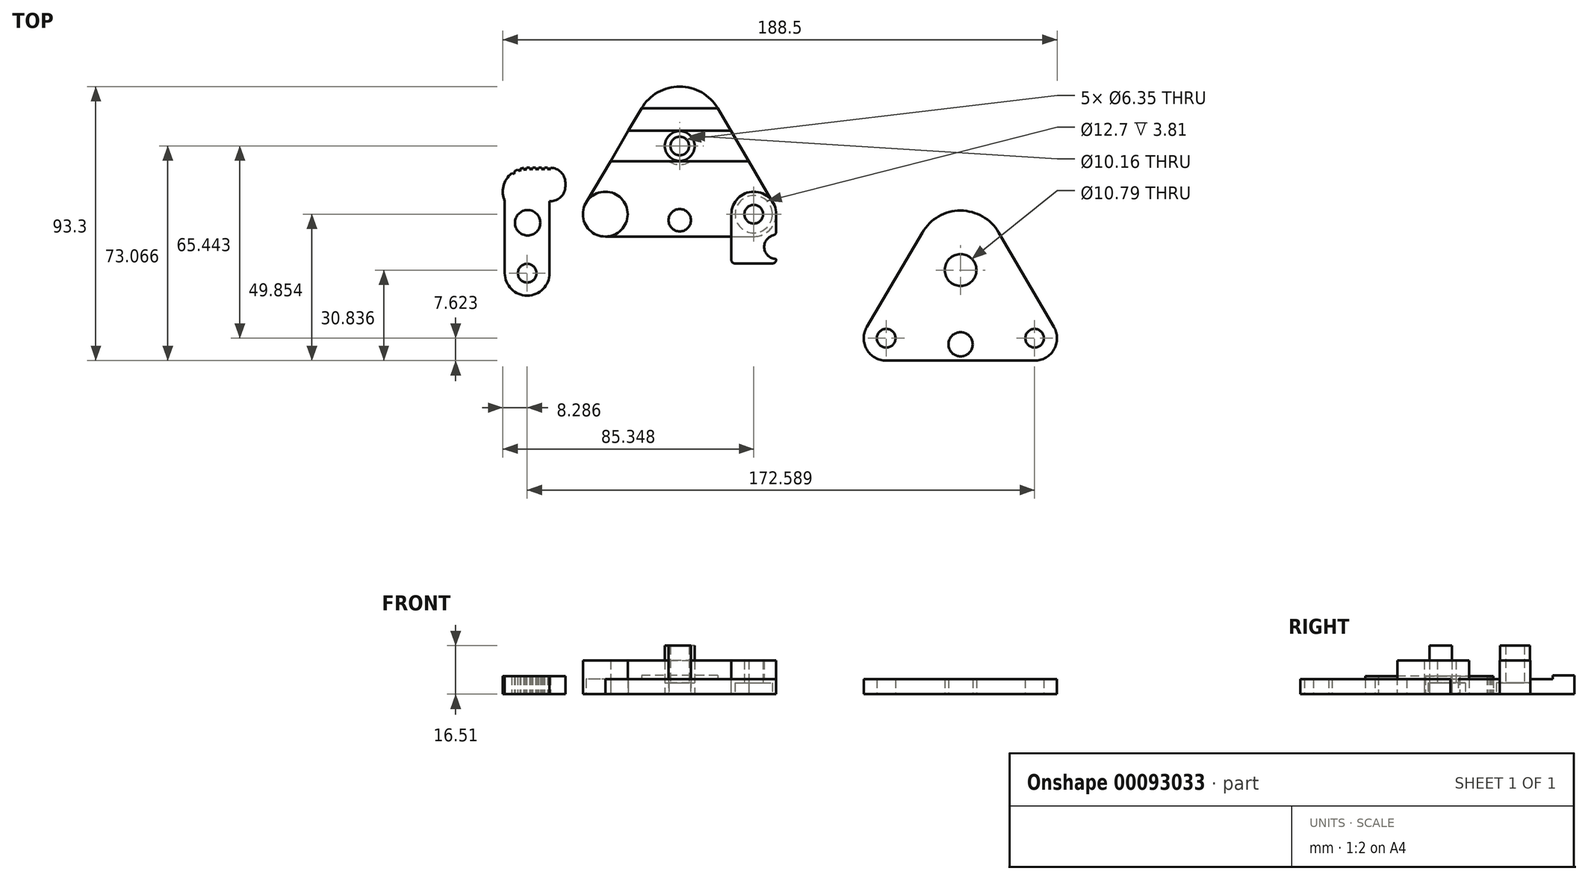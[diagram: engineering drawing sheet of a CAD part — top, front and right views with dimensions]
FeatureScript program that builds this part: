
annotation { "Feature Type Name" : "Feature", "Feature Type Description" : "" }
export const myFeature = defineFeature(function(context is Context, id is Id, definition is map)
    precondition{}
    {
        {
            var Q0;
            Q0=qCreatedBy(makeId("Top.planeOp"),FACE);
            var sketch = newSketch(context, id + "F0", { "sketchPlane" : qUnion([Q0])});
            skPoint(sketch, "E0.middle", {"position": v(0, 0) * mm});
            skLineSegment(sketch, "E1", {"start": v(-25.32, -38.25) * mm, "end": v(25.18, -38.25) * mm});
            skLineSegment(sketch, "E2", {"start": v(31.76, -26.78) * mm, "end": v(12.96, 5.36) * mm});
            skLineSegment(sketch, "E3", {"start": v(-13, 5.39) * mm, "end": v(-31.89, -26.77) * mm});
            skPoint(sketch, "E4.visualSharp", {"position": v(-38.63, -38.25) * mm});
            skArc(sketch, "E4.filletArc", {"start": v(-31.89, -26.77) * mm, "mid": v(-31.93, -34.41) * mm, "end": v(-25.32, -38.25) * mm});
            skPoint(sketch, "E5.visualSharp", {"position": v(38.46, -38.25) * mm});
            skArc(sketch, "E5.filletArc", {"start": v(25.18, -38.25) * mm, "mid": v(31.79, -34.42) * mm, "end": v(31.76, -26.78) * mm});
            skPoint(sketch, "E6.visualSharp", {"position": v(0, 27.54) * mm});
            skArc(sketch, "E6.filletArc", {"start": v(12.96, 5.36) * mm, "mid": v(-0.01, 12.82) * mm, "end": v(-13, 5.39) * mm});
            skLineSegment(sketch, "E7", {"start": v(12.96, 5.36) * mm, "end": v(-13, 5.39) * mm});
            skPoint(sketch, "E8", {"position": v(0, -2.24) * mm});
            skLineSegment(sketch, "E9", {"start": v(-17.48, -2.23) * mm, "end": v(17.41, -2.24) * mm});
            skPoint(sketch, "E10", {"position": v(0, -12.58) * mm});
            skCircle(sketch, "E11", {"center": v(0, -32.68) * mm, "radius": 3.81 * mm});
            skCircle(sketch, "E12", {"center": v(25.18, -30.63) * mm, "radius": 3.18 * mm});
            skCircle(sketch, "E13", {"center": v(-25.32, -30.63) * mm, "radius": 3.18 * mm});
            skLineSegment(sketch, "E14", {"start": v(-7.77, -25.38) * mm, "end": v(7.27, -25.38) * mm, "construction": true});
            skLineSegment(sketch, "E15", {"start": v(-0.37, -13.98) * mm, "end": v(-0.82, -14.9) * mm, "construction": true});
            skLineSegment(sketch, "E16", {"start": v(-0.82, -14.9) * mm, "end": v(-1.4, -14.06) * mm, "construction": true});
            skLineSegment(sketch, "E17", {"start": v(-2.4, -14.27) * mm, "end": v(-2.63, -15.26) * mm, "construction": true});
            skLineSegment(sketch, "E18", {"start": v(-2.63, -15.26) * mm, "end": v(-3.42, -14.62) * mm, "construction": true});
            skLineSegment(sketch, "E19", {"start": v(-4.44, -15.13) * mm, "end": v(-4.48, -16.14) * mm, "construction": true});
            skLineSegment(sketch, "E20", {"start": v(-4.48, -16.14) * mm, "end": v(-5.45, -15.84) * mm, "construction": true});
            skArc(sketch, "E21.trimOffspring", {"start": v(-1.4, -14.06) * mm, "mid": v(-1.9, -14.15) * mm, "end": v(-2.4, -14.27) * mm, "construction": true});
            skArc(sketch, "E22.trimOffspring", {"start": v(-3.42, -14.62) * mm, "mid": v(-3.94, -14.85) * mm, "end": v(-4.44, -15.13) * mm, "construction": true});
            skArc(sketch, "E23.trimOffspring", {"start": v(-5.45, -15.84) * mm, "mid": v(-8.2, -20.23) * mm, "end": v(-7.77, -25.38) * mm, "construction": true});
            skLineSegment(sketch, "E24", {"start": v(7.27, -25.38) * mm, "end": v(7.73, -25.38) * mm, "construction": true});
            skLineSegment(sketch, "E25", {"start": v(12.81, -20.3) * mm, "end": v(12.81, -19.06) * mm, "construction": true});
            skLineSegment(sketch, "E26", {"start": v(0, -13.98) * mm, "end": v(0.64, -13.98) * mm, "construction": true});
            skArc(sketch, "E27.filletArc", {"start": v(12.81, -19.06) * mm, "mid": v(11.32, -15.47) * mm, "end": v(7.73, -13.98) * mm, "construction": true});
            skLineSegment(sketch, "E28", {"start": v(-0.37, -13.98) * mm, "end": v(0, -13.98) * mm, "construction": true});
            skLineSegment(sketch, "E29", {"start": v(0.64, -13.98) * mm, "end": v(1.15, -14.86) * mm, "construction": true});
            skLineSegment(sketch, "E30", {"start": v(1.15, -14.86) * mm, "end": v(1.66, -13.98) * mm, "construction": true});
            skLineSegment(sketch, "E31", {"start": v(2.67, -13.98) * mm, "end": v(3.18, -14.86) * mm, "construction": true});
            skLineSegment(sketch, "E32", {"start": v(3.18, -14.86) * mm, "end": v(3.69, -13.98) * mm, "construction": true});
            skLineSegment(sketch, "E33", {"start": v(4.7, -13.98) * mm, "end": v(5.21, -14.86) * mm, "construction": true});
            skLineSegment(sketch, "E34", {"start": v(5.21, -14.86) * mm, "end": v(5.72, -13.98) * mm, "construction": true});
            skLineSegment(sketch, "E35", {"start": v(6.74, -13.98) * mm, "end": v(7.25, -14.86) * mm, "construction": true});
            skLineSegment(sketch, "E36", {"start": v(7.25, -14.86) * mm, "end": v(7.75, -13.98) * mm, "construction": true});
            skLineSegment(sketch, "E37.trimOffspring", {"start": v(5.72, -13.98) * mm, "end": v(6.74, -13.98) * mm, "construction": true});
            skLineSegment(sketch, "E38.trimOffspring", {"start": v(3.69, -13.98) * mm, "end": v(4.7, -13.98) * mm, "construction": true});
            skLineSegment(sketch, "E39.trimOffspring", {"start": v(1.66, -13.98) * mm, "end": v(2.67, -13.98) * mm, "construction": true});
            skLineSegment(sketch, "E40.bottom", {"start": v(-7.77, -25.38) * mm, "end": v(7.47, -25.38) * mm, "construction": true});
            skLineSegment(sketch, "E40.top", {"start": v(-0.15, -57.3) * mm, "end": v(-0.15, -57.3) * mm});
            skLineSegment(sketch, "E40.left", {"start": v(-7.77, -25.38) * mm, "end": v(-7.77, -49.68) * mm, "construction": true});
            skLineSegment(sketch, "E40.right", {"start": v(7.47, -25.38) * mm, "end": v(7.47, -49.68) * mm, "construction": true});
            skLineSegment(sketch, "E41", {"start": v(-23.56, -12.58) * mm, "end": v(23.46, -12.58) * mm});
            skPoint(sketch, "E42.visualSharp", {"position": v(12.81, -25.38) * mm});
            skArc(sketch, "E42.filletArc", {"start": v(7.73, -25.38) * mm, "mid": v(11.32, -23.9) * mm, "end": v(12.81, -20.3) * mm, "construction": true});
            skCircle(sketch, "E43", {"center": v(0, -32.68) * mm, "radius": 4.32 * mm, "construction": true});
            skPoint(sketch, "E44.visualSharp", {"position": v(-7.77, -57.3) * mm});
            skArc(sketch, "E44.filletArc", {"start": v(-7.77, -49.68) * mm, "mid": v(-5.53, -55.06) * mm, "end": v(-0.15, -57.3) * mm, "construction": true});
            skPoint(sketch, "E45.visualSharp", {"position": v(7.47, -57.3) * mm});
            skArc(sketch, "E45.filletArc", {"start": v(-0.15, -57.3) * mm, "mid": v(5.24, -55.06) * mm, "end": v(7.47, -49.68) * mm, "construction": true});
            skCircle(sketch, "E46", {"center": v(-0.15, -49.68) * mm, "radius": 3.18 * mm, "construction": true});
            skCircle(sketch, "E47", {"center": v(25.18, -30.63) * mm, "radius": 7.62 * mm});
            skCircle(sketch, "E48", {"center": v(-25.32, -30.63) * mm, "radius": 7.62 * mm});
            skPoint(sketch, "E49", {"position": v(0, -7.41) * mm});
            skCircle(sketch, "E50", {"center": v(0, -7.41) * mm, "radius": 3.18 * mm});
            skLineSegment(sketch, "E51", {"start": v(32.8, -30.63) * mm, "end": v(32.8, -36.58) * mm});
            skLineSegment(sketch, "E52", {"start": v(31.53, -47.41) * mm, "end": v(18.83, -47.41) * mm});
            skLineSegment(sketch, "E53", {"start": v(17.56, -30.63) * mm, "end": v(17.56, -46.14) * mm});
            skArc(sketch, "E54", {"start": v(31.83, -37.81) * mm, "mid": v(28.74, -42.14) * mm, "end": v(32.56, -45.83) * mm});
            skLineSegment(sketch, "E55.trimOffspring", {"start": v(32.8, -46.09) * mm, "end": v(32.8, -46.14) * mm});
            skPoint(sketch, "E56.visualSharp", {"position": v(17.56, -47.41) * mm});
            skArc(sketch, "E56.filletArc", {"start": v(17.56, -46.14) * mm, "mid": v(17.93, -47.04) * mm, "end": v(18.83, -47.41) * mm});
            skPoint(sketch, "E57.visualSharp", {"position": v(32.8, -47.41) * mm});
            skArc(sketch, "E57.filletArc", {"start": v(31.53, -47.41) * mm, "mid": v(32.43, -47.04) * mm, "end": v(32.8, -46.14) * mm});
            skPoint(sketch, "E58.visualSharp", {"position": v(32.8, -37.7) * mm});
            skArc(sketch, "E58.filletArc", {"start": v(31.83, -37.81) * mm, "mid": v(32.53, -37.36) * mm, "end": v(32.8, -36.58) * mm});
            skPoint(sketch, "E59.visualSharp", {"position": v(32.8, -45.84) * mm});
            skArc(sketch, "E59.filletArc", {"start": v(32.8, -46.09) * mm, "mid": v(32.73, -45.91) * mm, "end": v(32.56, -45.83) * mm});
            skCircle(sketch, "E60", {"center": v(0, -7.41) * mm, "radius": 5.08 * mm});
            skSolve(sketch);
        }
        {
            var Q0;
            Q0=makeQuery(id+"F0.imprint","IMPRINT",FACE,{"disambiguationData":[TD([[makeQuery(id+"F0.imprint","IMPRINT",EDGE,{"derivedFrom":sQuery(id+"F0.wireOp",EDGE,"E11")}),-1.0]])]});
            var sketch = newSketch(context, id + "F1", { "sketchPlane" : qUnion([Q0])});
            skLineSegment(sketch, "E61", {"start": v(-59.5, -26.24) * mm, "end": v(-44.47, -26.24) * mm});
            skLineSegment(sketch, "E62", {"start": v(-52.11, -14.83) * mm, "end": v(-52.55, -15.75) * mm});
            skLineSegment(sketch, "E63", {"start": v(-52.55, -15.75) * mm, "end": v(-53.13, -14.91) * mm});
            skLineSegment(sketch, "E64", {"start": v(-54.15, -15.12) * mm, "end": v(-54.37, -16.11) * mm});
            skLineSegment(sketch, "E65", {"start": v(-54.37, -16.11) * mm, "end": v(-55.16, -15.47) * mm});
            skLineSegment(sketch, "E66", {"start": v(-56.18, -15.98) * mm, "end": v(-56.22, -17) * mm});
            skLineSegment(sketch, "E67", {"start": v(-56.22, -17) * mm, "end": v(-57.2, -16.7) * mm});
            skArc(sketch, "E68.trimOffspring", {"start": v(-53.13, -14.91) * mm, "mid": v(-53.64, -15) * mm, "end": v(-54.15, -15.12) * mm});
            skArc(sketch, "E69.trimOffspring", {"start": v(-55.16, -15.47) * mm, "mid": v(-55.68, -15.7) * mm, "end": v(-56.18, -15.98) * mm});
            skArc(sketch, "E70.trimOffspring", {"start": v(-57.2, -16.7) * mm, "mid": v(-59.94, -21.08) * mm, "end": v(-59.5, -26.24) * mm});
            skLineSegment(sketch, "E71", {"start": v(-44.47, -26.24) * mm, "end": v(-44, -26.24) * mm});
            skLineSegment(sketch, "E72", {"start": v(-38.93, -21.16) * mm, "end": v(-38.93, -19.91) * mm});
            skLineSegment(sketch, "E73", {"start": v(-51.74, -14.83) * mm, "end": v(-51.1, -14.83) * mm});
            skArc(sketch, "E74.filletArc", {"start": v(-38.93, -19.91) * mm, "mid": v(-40.42, -16.32) * mm, "end": v(-44, -14.83) * mm});
            skLineSegment(sketch, "E75", {"start": v(-52.11, -14.83) * mm, "end": v(-51.74, -14.83) * mm});
            skLineSegment(sketch, "E76", {"start": v(-51.1, -14.83) * mm, "end": v(-50.59, -15.71) * mm});
            skLineSegment(sketch, "E77", {"start": v(-50.59, -15.71) * mm, "end": v(-50.08, -14.83) * mm});
            skLineSegment(sketch, "E78", {"start": v(-49.07, -14.83) * mm, "end": v(-48.56, -15.71) * mm});
            skLineSegment(sketch, "E79", {"start": v(-48.56, -15.71) * mm, "end": v(-48.05, -14.83) * mm});
            skLineSegment(sketch, "E80", {"start": v(-47.03, -14.83) * mm, "end": v(-46.53, -15.71) * mm});
            skLineSegment(sketch, "E81", {"start": v(-46.53, -15.71) * mm, "end": v(-46.02, -14.83) * mm});
            skLineSegment(sketch, "E82", {"start": v(-45, -14.83) * mm, "end": v(-44.5, -15.71) * mm});
            skLineSegment(sketch, "E83", {"start": v(-44.5, -15.71) * mm, "end": v(-43.99, -14.83) * mm});
            skLineSegment(sketch, "E84.trimOffspring", {"start": v(-46.02, -14.83) * mm, "end": v(-45, -14.83) * mm});
            skLineSegment(sketch, "E85.trimOffspring", {"start": v(-48.05, -14.83) * mm, "end": v(-47.03, -14.83) * mm});
            skLineSegment(sketch, "E86.trimOffspring", {"start": v(-50.08, -14.83) * mm, "end": v(-49.07, -14.83) * mm});
            skLineSegment(sketch, "E87.bottom", {"start": v(-59.5, -26.24) * mm, "end": v(-44.26, -26.24) * mm});
            skLineSegment(sketch, "E87.left", {"start": v(-59.5, -26.24) * mm, "end": v(-59.5, -50.71) * mm});
            skLineSegment(sketch, "E87.right", {"start": v(-44.26, -26.24) * mm, "end": v(-44.26, -50.71) * mm});
            skPoint(sketch, "E88.visualSharp", {"position": v(-38.93, -26.24) * mm});
            skArc(sketch, "E88.filletArc", {"start": v(-44, -26.24) * mm, "mid": v(-40.42, -24.75) * mm, "end": v(-38.93, -21.16) * mm});
            skCircle(sketch, "E89", {"center": v(-51.74, -33.55) * mm, "radius": 4.32 * mm});
            skPoint(sketch, "E90.visualSharp", {"position": v(-59.5, -58.33) * mm});
            skArc(sketch, "E90.filletArc", {"start": v(-59.5, -50.71) * mm, "mid": v(-57.27, -56.1) * mm, "end": v(-51.88, -58.33) * mm});
            skPoint(sketch, "E91.visualSharp", {"position": v(-44.26, -58.33) * mm});
            skArc(sketch, "E91.filletArc", {"start": v(-51.88, -58.33) * mm, "mid": v(-46.5, -56.1) * mm, "end": v(-44.26, -50.71) * mm});
            skCircle(sketch, "E92", {"center": v(-51.88, -50.71) * mm, "radius": 3.18 * mm});
            skSolve(sketch);
        }
        {
            var Q0;
            Q0=makeQuery(id+"F0.imprint","IMPRINT",FACE,{"disambiguationData":[TD([[makeQuery(id+"F0.imprint","IMPRINT",EDGE,{"derivedFrom":sQuery(id+"F0.wireOp",EDGE,"E11")}),-1.0]])]});
            var Q1;
            {var subQ0=sQuery(id+"F0.wireOp",EDGE,"E7");Q1=makeQuery(id+"F0.imprint","IMPRINT",FACE,{"disambiguationData":[TD([[makeQuery(id+"F0.imprint","IMPRINT",EDGE,{"derivedFrom":subQ0}),1.0]])]});}
            var Q2;
            {var subQ0=sQuery(id+"F0.wireOp",EDGE,"E47");var subQ1=sQuery(id+"F0.wireOp",EDGE,"E1");var subQ2=makeQuery(id+"F0.imprint","INTERSECT",VERTEX,{"derivedFrom":[subQ1,subQ0]});Q2=makeQuery(id+"F0.imprint","IMPRINT",FACE,{"disambiguationData":[TD([[makeQuery(id+"F0.imprint","IMPRINT",EDGE,{"disambiguationData":[TD([[subQ2,1.0]])],"derivedFrom":subQ1}),1.0]])]});}
            extrude(context, id + "F2", {"entities" : qUnion([Q0, Q1, Q2]), "depth" : 5.08 * mm});
        }
        {
            var Q0;
            {var subQ1=sQuery(id+"F0.wireOp",EDGE,"E9");Q0=makeQuery(id+"F0.imprint","IMPRINT",FACE,{"disambiguationData":[TD([[makeQuery(id+"F0.imprint","IMPRINT",EDGE,{"derivedFrom":subQ1}),-1.0]])]});}
            var Q1;
            Q1=makeQuery(id+"F0.imprint","IMPRINT",FACE,{"disambiguationData":[TD([[makeQuery(id+"F0.imprint","IMPRINT",EDGE,{"derivedFrom":sQuery(id+"F0.wireOp",EDGE,"E13")}),-1.0]])]});
            var Q2;
            Q2=makeQuery(id+"F0.imprint","IMPRINT",FACE,{"disambiguationData":[TD([[makeQuery(id+"F0.imprint","IMPRINT",EDGE,{"derivedFrom":sQuery(id+"F0.wireOp",EDGE,"E12")}),-1.0]])]});
            var Q3;
            {var subQ0=sQuery(id+"F0.wireOp",EDGE,"E47");var subQ1=sQuery(id+"F0.wireOp",EDGE,"E1");var subQ2=makeQuery(id+"F0.imprint","INTERSECT",VERTEX,{"derivedFrom":[subQ1,subQ0]});Q3=makeQuery(id+"F0.imprint","IMPRINT",FACE,{"disambiguationData":[TD([[makeQuery(id+"F0.imprint","IMPRINT",EDGE,{"disambiguationData":[TD([[subQ2,1.0]])],"derivedFrom":subQ1}),1.0]])]});}
            var Q4;
            Q4=makeQuery(id+"F0.imprint","IMPRINT",FACE,{"disambiguationData":[TD([[makeQuery(id+"F0.imprint","IMPRINT",EDGE,{"derivedFrom":sQuery(id+"F0.wireOp",EDGE,"E12")}),1.0]])]});
            var Q5;
            Q5=makeQuery(id+"F0.imprint","IMPRINT",FACE,{"disambiguationData":[TD([[makeQuery(id+"F0.imprint","IMPRINT",EDGE,{"derivedFrom":sQuery(id+"F0.wireOp",EDGE,"E13")}),1.0]])]});
            extrude(context, id + "F3", {"entities" : qUnion([Q0, Q1, Q2, Q3, Q4, Q5]), "depth" : 11.43 * mm});
        }
        {
            var Q0;
            Q0=makeQuery(id+"F0.imprint","IMPRINT",FACE,{"disambiguationData":[TD([[makeQuery(id+"F0.imprint","IMPRINT",EDGE,{"derivedFrom":sQuery(id+"F0.wireOp",EDGE,"E11")}),1.0]])]});
            var Q1;
            Q1=makeQuery(id+"F0.imprint","IMPRINT",FACE,{"disambiguationData":[TD([[makeQuery(id+"F0.imprint","IMPRINT",EDGE,{"derivedFrom":sQuery(id+"F0.wireOp",EDGE,"E50")}),-1.0]])]});
            var Q2;
            Q2=makeQuery(id+"F0.imprint","IMPRINT",FACE,{"disambiguationData":[TD([[makeQuery(id+"F0.imprint","IMPRINT",EDGE,{"derivedFrom":sQuery(id+"F0.wireOp",EDGE,"E50")}),1.0]])]});
            extrude(context, id + "F4", {"entities" : qUnion([Q0, Q1, Q2]), "depth" : 16.5 * mm});
        }
        {
            var Q0;
            Q0=makeQuery(id+"F0.imprint","IMPRINT",FACE,{"disambiguationData":[TD([[makeQuery(id+"F0.imprint","IMPRINT",EDGE,{"derivedFrom":sQuery(id+"F0.wireOp",EDGE,"E6.filletArc")}),1.0]])]});
            extrude(context, id + "F5", {"entities" : qUnion([Q0]), "operationType" : NewBodyOperationType.ADD, "depth" : 6.35 * mm});
        }
        {
            var Q0;
            {var subQ3=sQuery(id+"F0.wireOp",EDGE,"E51");Q0=makeQuery(id+"F0.imprint","IMPRINT",FACE,{"disambiguationData":[TD([[makeQuery(id+"F0.imprint","IMPRINT",EDGE,{"derivedFrom":subQ3}),-1.0]])]});}
            extrude(context, id + "F6", {"entities" : qUnion([Q0]), "operationType" : NewBodyOperationType.ADD, "depth" : 11.43 * mm, "hasSecondDirection" : true, "secondDirectionOppositeDirection" : false, "secondDirectionDepth" : 5.08 * mm});
        }
        {
            var Q0;
            Q0=makeQuery(id+"F1.imprint","IMPRINT",FACE,{"disambiguationData":[TD([[makeQuery(id+"F1.imprint","IMPRINT",EDGE,{"derivedFrom":sQuery(id+"F1.wireOp",EDGE,"E62")}),1.0]])]});
            var Q1;
            {var subQ3=sQuery(id+"F1.wireOp",EDGE,"E87.left");Q1=makeQuery(id+"F1.imprint","IMPRINT",FACE,{"disambiguationData":[TD([[makeQuery(id+"F1.imprint","IMPRINT",EDGE,{"derivedFrom":subQ3}),1.0]])]});}
            extrude(context, id + "F7", {"entities" : qUnion([Q0, Q1]), "depth" : 6.1 * mm});
        }
        {
            var Q0;
            Q0=qCreatedBy(makeId("Top.planeOp"),FACE);
            var sketch = newSketch(context, id + "F8", { "sketchPlane" : qUnion([Q0])});
            skLineSegment(sketch, "E93", {"start": v(70.21, -80.48) * mm, "end": v(120.7, -80.48) * mm});
            skLineSegment(sketch, "E94", {"start": v(127.28, -69.01) * mm, "end": v(108.5, -36.87) * mm});
            skLineSegment(sketch, "E95", {"start": v(82.52, -36.84) * mm, "end": v(63.64, -69) * mm});
            skPoint(sketch, "E96.visualSharp", {"position": v(56.9, -80.48) * mm});
            skArc(sketch, "E96.filletArc", {"start": v(63.64, -69) * mm, "mid": v(63.6, -76.64) * mm, "end": v(70.21, -80.48) * mm});
            skPoint(sketch, "E97.visualSharp", {"position": v(133.99, -80.48) * mm});
            skArc(sketch, "E97.filletArc", {"start": v(120.7, -80.48) * mm, "mid": v(127.32, -76.65) * mm, "end": v(127.28, -69.01) * mm});
            skPoint(sketch, "E98.visualSharp", {"position": v(95.53, -14.7) * mm});
            skArc(sketch, "E98.filletArc", {"start": v(108.5, -36.87) * mm, "mid": v(95.51, -29.41) * mm, "end": v(82.52, -36.84) * mm});
            skCircle(sketch, "E99", {"center": v(95.53, -74.91) * mm, "radius": 4.13 * mm});
            skCircle(sketch, "E100", {"center": v(120.7, -72.86) * mm, "radius": 3.18 * mm});
            skCircle(sketch, "E101", {"center": v(70.21, -72.86) * mm, "radius": 3.18 * mm});
            skPoint(sketch, "E102", {"position": v(95.53, -49.64) * mm});
            skPoint(sketch, "E103.visualSharp", {"position": v(128.33, -79.93) * mm});
            skCircle(sketch, "E104", {"center": v(95.53, -49.64) * mm, "radius": 5.4 * mm});
            skPoint(sketch, "E105.end.orphan", {"position": v(112.94, -44.48) * mm});
            skPoint(sketch, "E105.start.orphan", {"position": v(78.05, -44.46) * mm});
            skPoint(sketch, "E106.orphan", {"position": v(71.97, -54.81) * mm});
            skPoint(sketch, "E107.end.orphan", {"position": v(118.98, -54.81) * mm});
            skSolve(sketch);
        }
        {
            var Q0;
            {var subQ1=sQuery(id+"F8.wireOp",EDGE,"216794e6-27fa-4e69-877c-28185c22a6c9");Q0=makeQuery(id+"F8.imprint","IMPRINT",FACE,{"disambiguationData":[TD([[makeQuery(id+"F8.imprint","IMPRINT",EDGE,{"derivedFrom":subQ1}),1.0]])]});}
            var Q1;
            {var subQ1=sQuery(id+"F8.wireOp",EDGE,"bfd4ebca-ad6c-44b5-a8af-35f49ae3cf0c");Q1=makeQuery(id+"F8.imprint","IMPRINT",FACE,{"disambiguationData":[TD([[makeQuery(id+"F8.imprint","IMPRINT",EDGE,{"derivedFrom":subQ1}),1.0]])]});}
            var Q2;
            Q2=makeQuery(id+"F8.imprint","IMPRINT",FACE,{"disambiguationData":[TD([[makeQuery(id+"F8.imprint","IMPRINT",EDGE,{"derivedFrom":makeQuery(id+"F3.opExtrude","CAP_EDGE",EDGE,{"disambiguationData":[OSD([sQuery(id+"F0.wireOp",EDGE,"E50")])],"isStart":false})}),1.0]])]});
            var Q3;
            Q3=makeQuery(id+"F8.imprint","IMPRINT",FACE,{"disambiguationData":[TD([[makeQuery(id+"F8.imprint","IMPRINT",EDGE,{"derivedFrom":sQuery(id+"F8.wireOp",EDGE,"b530ac93-75ae-482a-9c66-041d02c707ac")}),-1.0]])]});
            var Q4;
            {var subQ0=sQuery(id+"F8.wireOp",EDGE,"d28c21e8-73c2-4f8c-b565-6b58b0dd52e0");var subQ1=makeQuery(id+"F3.opExtrude","CAP_EDGE",EDGE,{"disambiguationData":[OSD([sQuery(id+"F0.wireOp",EDGE,"E2")])],"isStart":false});var subQ2=makeQuery(id+"F8.imprint","INTERSECT",VERTEX,{"derivedFrom":[subQ1,subQ0]});Q4=makeQuery(id+"F8.imprint","IMPRINT",FACE,{"disambiguationData":[TD([[makeQuery(id+"F8.imprint","IMPRINT",EDGE,{"disambiguationData":[TD([[subQ2,-1.0]])],"derivedFrom":subQ0}),1.0]])]});}
            var Q5;
            Q5=makeQuery(id+"F8.imprint","IMPRINT",FACE,{"disambiguationData":[TD([[makeQuery(id+"F8.imprint","IMPRINT",EDGE,{"derivedFrom":sQuery(id+"F8.wireOp",EDGE,"48c16e6e-6f29-480b-870d-e4ed0377c5a1")}),-1.0]])]});
            var Q6;
            {var subQ0=sQuery(id+"F8.wireOp",EDGE,"bfb3cdb1-9707-4c23-9635-bff32e19fff3");var subQ1=makeQuery(id+"F3.opExtrude","CAP_EDGE",EDGE,{"disambiguationData":[OSD([sQuery(id+"F0.wireOp",EDGE,"E3")])],"isStart":false});var subQ2=makeQuery(id+"F8.imprint","INTERSECT",VERTEX,{"derivedFrom":[subQ1,subQ0]});Q6=makeQuery(id+"F8.imprint","IMPRINT",FACE,{"disambiguationData":[TD([[makeQuery(id+"F8.imprint","IMPRINT",EDGE,{"disambiguationData":[TD([[subQ2,1.0]])],"derivedFrom":subQ0}),1.0]])]});}
            var Q7;
            Q7=makeQuery(id+"F8.imprint","IMPRINT",FACE,{"disambiguationData":[TD([[makeQuery(id+"F8.imprint","IMPRINT",EDGE,{"derivedFrom":sQuery(id+"F8.wireOp",EDGE,"E93")}),1.0]])]});
            extrude(context, id + "F9", {"entities" : qUnion([Q0, Q1, Q2, Q3, Q4, Q5, Q6, Q7]), "depth" : 5.08 * mm});
        }
        {
            var Q0;
            Q0=sQuery(id+"F0.wireOp",VERTEX,"E4.filletArc.center");
            var Q1;
            Q1=sQuery(id+"F0.wireOp",VERTEX,"E5.filletArc.center");
            var Q2;
            Q2=sQuery(id+"F0.wireOp",VERTEX,"E49");
            var Q3;
            Q3=makeQuery(id+"F2.opExtrude","SWEPT_BODY",BODY,{"disambiguationData":[OSD([sQuery(id+"F0.wireOp",EDGE,"E1"),sQuery(id+"F0.wireOp",EDGE,"E2"),sQuery(id+"F0.wireOp",EDGE,"E3"),sQuery(id+"F0.wireOp",EDGE,"E11"),sQuery(id+"F0.wireOp",EDGE,"E41"),sQuery(id+"F0.wireOp",EDGE,"E47"),sQuery(id+"F0.wireOp",EDGE,"E48")])]});
            var Q4;
            Q4=makeQuery(id+"F4.opExtrude","SWEPT_BODY",BODY,{"disambiguationData":[OSD([sQuery(id+"F0.wireOp",EDGE,"E60")])]});
            hole(context, id + "F10", {"style" : HoleStyle.C_BORE, "endStyle" : HoleEndStyle.THROUGH, "oppositeDirection" : true, "holeDiameter" : 6.35 * mm, "cBoreDiameter" : 12.7 * mm, "cBoreDepth" : 3.8 * mm, "locations" : qUnion([Q0, Q1, Q2]), "scope" : qUnion([Q3, Q4]), "isTappedThrough" : true});
        }
    });
